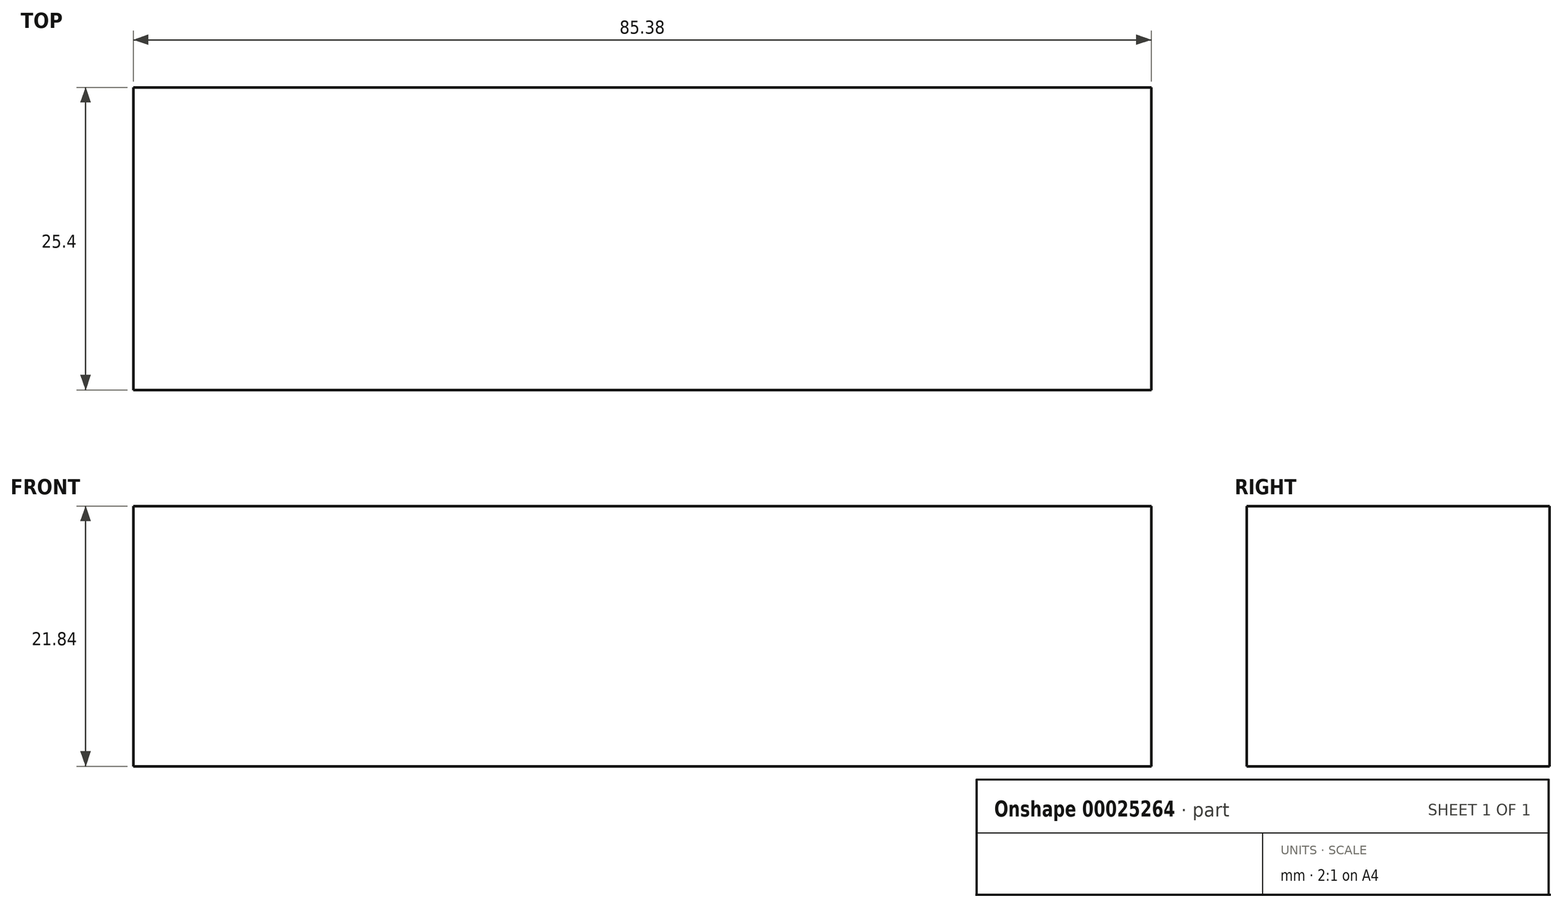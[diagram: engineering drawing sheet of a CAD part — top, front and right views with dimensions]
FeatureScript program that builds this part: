
annotation { "Feature Type Name" : "Feature", "Feature Type Description" : "" }
export const myFeature = defineFeature(function(context is Context, id is Id, definition is map)
    precondition{}
    {
        {
            var Q0;
            Q0=qCreatedBy(makeId("Front.planeOp"),FACE);
            var sketch = newSketch(context, id + "F0", { "sketchPlane" : qUnion([Q0])});
            skLineSegment(sketch, "E0", {"start": v(-40.94, 21.84) * mm, "end": v(-40.94, 0) * mm});
            skLineSegment(sketch, "E1", {"start": v(-40.94, 21.84) * mm, "end": v(44.44, 21.84) * mm});
            skLineSegment(sketch, "E2", {"start": v(44.44, 21.84) * mm, "end": v(44.44, 0) * mm});
            skLineSegment(sketch, "E3", {"start": v(44.44, 0) * mm, "end": v(-40.94, 0) * mm});
            skSolve(sketch);
        }
        {
            var Q0;
            Q0=makeQuery(id+"F0.imprint","IMPRINT",FACE,{"disambiguationData":[TD([[makeQuery(id+"F0.imprint","IMPRINT",EDGE,{"derivedFrom":sQuery(id+"F0.wireOp",EDGE,"E0")}),1.0]])]});
            extrude(context, id + "F1", {"entities" : qUnion([Q0]), "depth" : 25.4 * mm});
        }
    });
